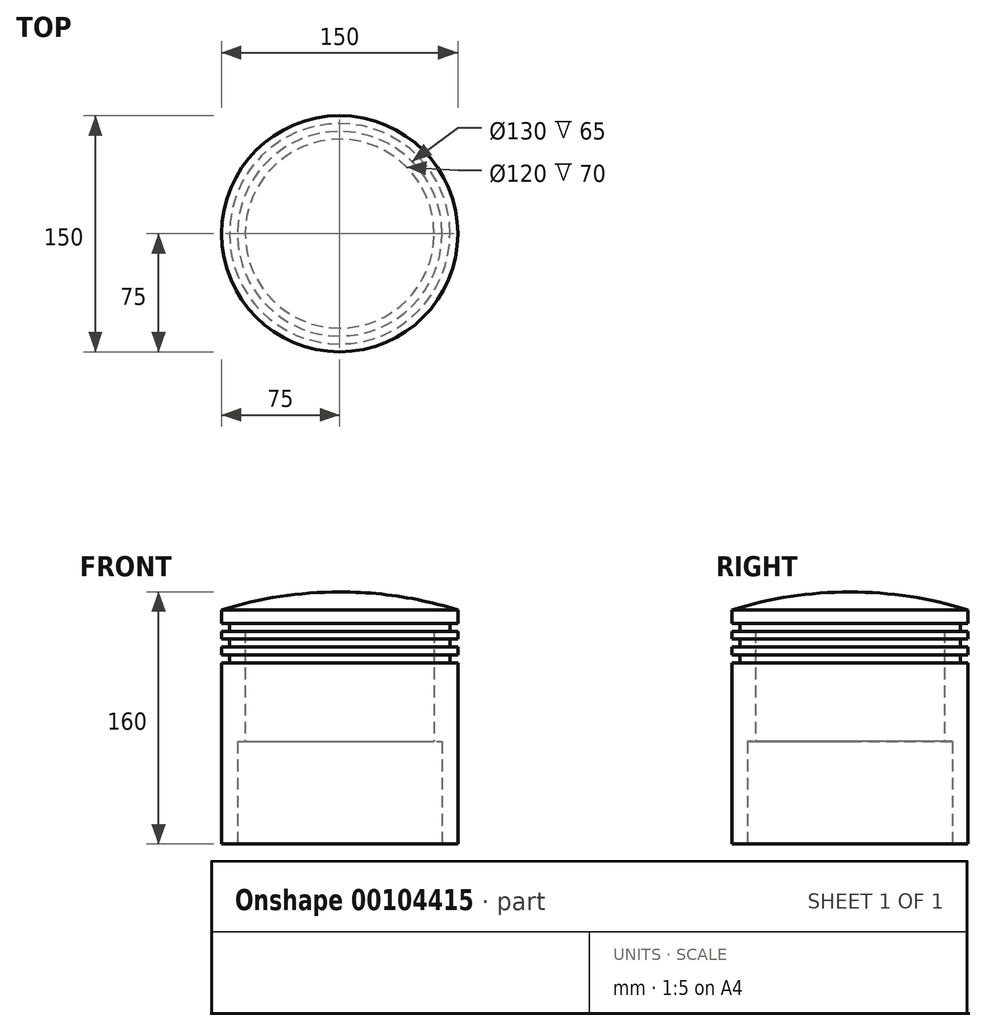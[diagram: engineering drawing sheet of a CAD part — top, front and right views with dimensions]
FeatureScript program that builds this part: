
annotation { "Feature Type Name" : "Feature", "Feature Type Description" : "" }
export const myFeature = defineFeature(function(context is Context, id is Id, definition is map)
    precondition{}
    {
        {
            var Q0;
            Q0=qCreatedBy(makeId("Front.planeOp"),FACE);
            var sketch = newSketch(context, id + "F0", { "sketchPlane" : qUnion([Q0])});
            skLineSegment(sketch, "E0", {"start": v(0, 0) * mm, "end": v(75, 0) * mm});
            skLineSegment(sketch, "E1", {"start": v(75, 0) * mm, "end": v(75, 148.48) * mm});
            skArc(sketch, "E2", {"start": v(75, 148.48) * mm, "mid": v(37.94, 157.1) * mm, "end": v(0, 160) * mm});
            skLineSegment(sketch, "E3", {"start": v(0, 0) * mm, "end": v(0, 160) * mm});
            skSolve(sketch);
        }
        {
            var Q0;
            Q0=makeQuery(id+"F0.imprint","IMPRINT",FACE,{"disambiguationData":[TD([[makeQuery(id+"F0.imprint","IMPRINT",EDGE,{"derivedFrom":sQuery(id+"F0.wireOp",EDGE,"E0")}),1.0]])]});
            var Q1;
            Q1=sQuery(id+"F0.wireOp",EDGE,"E3");
            revolve(context, id + "F1", {"entities" : qUnion([Q0]), "axis" : qUnion([Q1]), "revolveType" : RevolveType.FULL});
        }
        {
            var Q0;
            Q0=makeQuery(id+"F1.opRevolve","SWEPT_FACE",FACE,{"disambiguationData":[OSD([sQuery(id+"F0.wireOp",EDGE,"E0")])]});
            var sketch = newSketch(context, id + "F2", { "sketchPlane" : qUnion([Q0])});
            skCircle(sketch, "E4", {"center": v(0, 0) * mm, "radius": 65 * mm});
            skSolve(sketch);
        }
        {
            var Q0;
            Q0=makeQuery(id+"F2.imprint","IMPRINT",FACE,{"disambiguationData":[TD([[makeQuery(id+"F2.imprint","IMPRINT",EDGE,{"derivedFrom":sQuery(id+"F2.wireOp",EDGE,"E4")}),1.0]])]});
            var Q1;
            Q1=sQuery(id+"F2.wireOp",EDGE,"E4");
            extrude(context, id + "F3", {"entities" : qUnion([Q0]), "operationType" : NewBodyOperationType.REMOVE, "surfaceEntities" : qUnion([Q1]), "oppositeDirection" : true, "depth" : 65 * mm});
        }
        {
            var Q0;
            Q0=makeQuery(id+"F3.boolean.opBoolean","COPY",FACE,{"derivedFrom":makeQuery(id+"F3.opExtrude","CAP_FACE",FACE,{"disambiguationData":[OSD([sQuery(id+"F2.wireOp",EDGE,"E4")])],"isStart":false})});
            var sketch = newSketch(context, id + "F4", { "sketchPlane" : qUnion([Q0])});
            skCircle(sketch, "E5", {"center": v(0, 0) * mm, "radius": 60 * mm});
            skSolve(sketch);
        }
        {
            var Q0;
            Q0=makeQuery(id+"F4.imprint","IMPRINT",FACE,{"disambiguationData":[TD([[makeQuery(id+"F4.imprint","IMPRINT",EDGE,{"derivedFrom":sQuery(id+"F4.wireOp",EDGE,"E5")}),1.0]])]});
            extrude(context, id + "F5", {"entities" : qUnion([Q0]), "operationType" : NewBodyOperationType.REMOVE, "oppositeDirection" : true, "depth" : (135 - 65) * mm});
        }
        {
            var Q0;
            Q0=qCreatedBy(makeId("Front.planeOp"),FACE);
            var sketch = newSketch(context, id + "F6", { "sketchPlane" : qUnion([Q0])});
            skLineSegment(sketch, "E6.bottom", {"start": v(70, 130) * mm, "end": v(91.87, 130) * mm});
            skLineSegment(sketch, "E6.top", {"start": v(70, 125) * mm, "end": v(91.87, 125) * mm});
            skLineSegment(sketch, "E6.left", {"start": v(70, 130) * mm, "end": v(70, 125) * mm});
            skLineSegment(sketch, "E6.right", {"start": v(91.87, 130) * mm, "end": v(91.87, 125) * mm});
            skLineSegment(sketch, "E7.bottom", {"start": v(70, 140) * mm, "end": v(91.77, 140) * mm});
            skLineSegment(sketch, "E7.top", {"start": v(70, 135) * mm, "end": v(91.77, 135) * mm});
            skLineSegment(sketch, "E7.left", {"start": v(70, 140) * mm, "end": v(70, 135) * mm});
            skLineSegment(sketch, "E7.right", {"start": v(91.77, 140) * mm, "end": v(91.77, 135) * mm});
            skLineSegment(sketch, "E8.bottom", {"start": v(70, 120) * mm, "end": v(86.61, 120) * mm});
            skLineSegment(sketch, "E8.top", {"start": v(70, 115) * mm, "end": v(86.61, 115) * mm});
            skLineSegment(sketch, "E8.left", {"start": v(70, 120) * mm, "end": v(70, 115) * mm});
            skLineSegment(sketch, "E8.right", {"start": v(86.61, 120) * mm, "end": v(86.61, 115) * mm});
            skSolve(sketch);
        }
        {
            var Q0;
            Q0=makeQuery(id+"F6.imprint","IMPRINT",FACE,{"disambiguationData":[TD([[makeQuery(id+"F6.imprint","IMPRINT",EDGE,{"derivedFrom":sQuery(id+"F6.wireOp",EDGE,"E7.bottom")}),-1.0]])]});
            var Q1;
            Q1=makeQuery(id+"F6.imprint","IMPRINT",FACE,{"disambiguationData":[TD([[makeQuery(id+"F6.imprint","IMPRINT",EDGE,{"derivedFrom":sQuery(id+"F6.wireOp",EDGE,"E8.bottom")}),-1.0]])]});
            var Q2;
            Q2=makeQuery(id+"F6.imprint","IMPRINT",FACE,{"disambiguationData":[TD([[makeQuery(id+"F6.imprint","IMPRINT",EDGE,{"derivedFrom":sQuery(id+"F6.wireOp",EDGE,"E6.bottom")}),-1.0]])]});
            var Q3;
            Q3=makeQuery(id+"F3.boolean.opBoolean","COPY",FACE,{"derivedFrom":makeQuery(id+"F3.opExtrude","SWEPT_FACE",FACE,{"disambiguationData":[OSD([sQuery(id+"F2.wireOp",EDGE,"E4")])]})});
            revolve(context, id + "F7", {"operationType" : NewBodyOperationType.REMOVE, "entities" : qUnion([Q0, Q1, Q2]), "axis" : qUnion([Q3]), "revolveType" : RevolveType.FULL, "oppositeDirection" : true});
        }
    });
